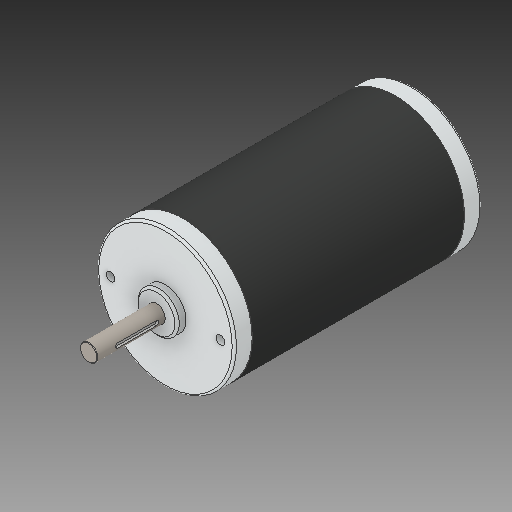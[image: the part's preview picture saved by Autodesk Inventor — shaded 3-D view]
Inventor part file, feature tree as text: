
AUTODESK INVENTOR PART (.ipt)
format: ipt  version: 2018 (Build 220112000, 112)  size: 165,888 bytes
history: native  units: in
note: dims shown in document units (in); Inventor stores cm internally (conversion verified against a paired STEP export)
features: fillet x1
ambient origin geometry x8: Origin, YZ Plane, XZ Plane, XY Plane, X Axis, Y Axis, Z Axis, Center Point
bodies: Solid1 (feature_tree)
feature tree (1):
  fillet  "Fillet5"  [1 undecoded]
note: 1 required parameter value undecoded (feature->parameter linkage not recoverable at this tier; creation-order binding heuristic only, values carry confidence <= 0.55)
